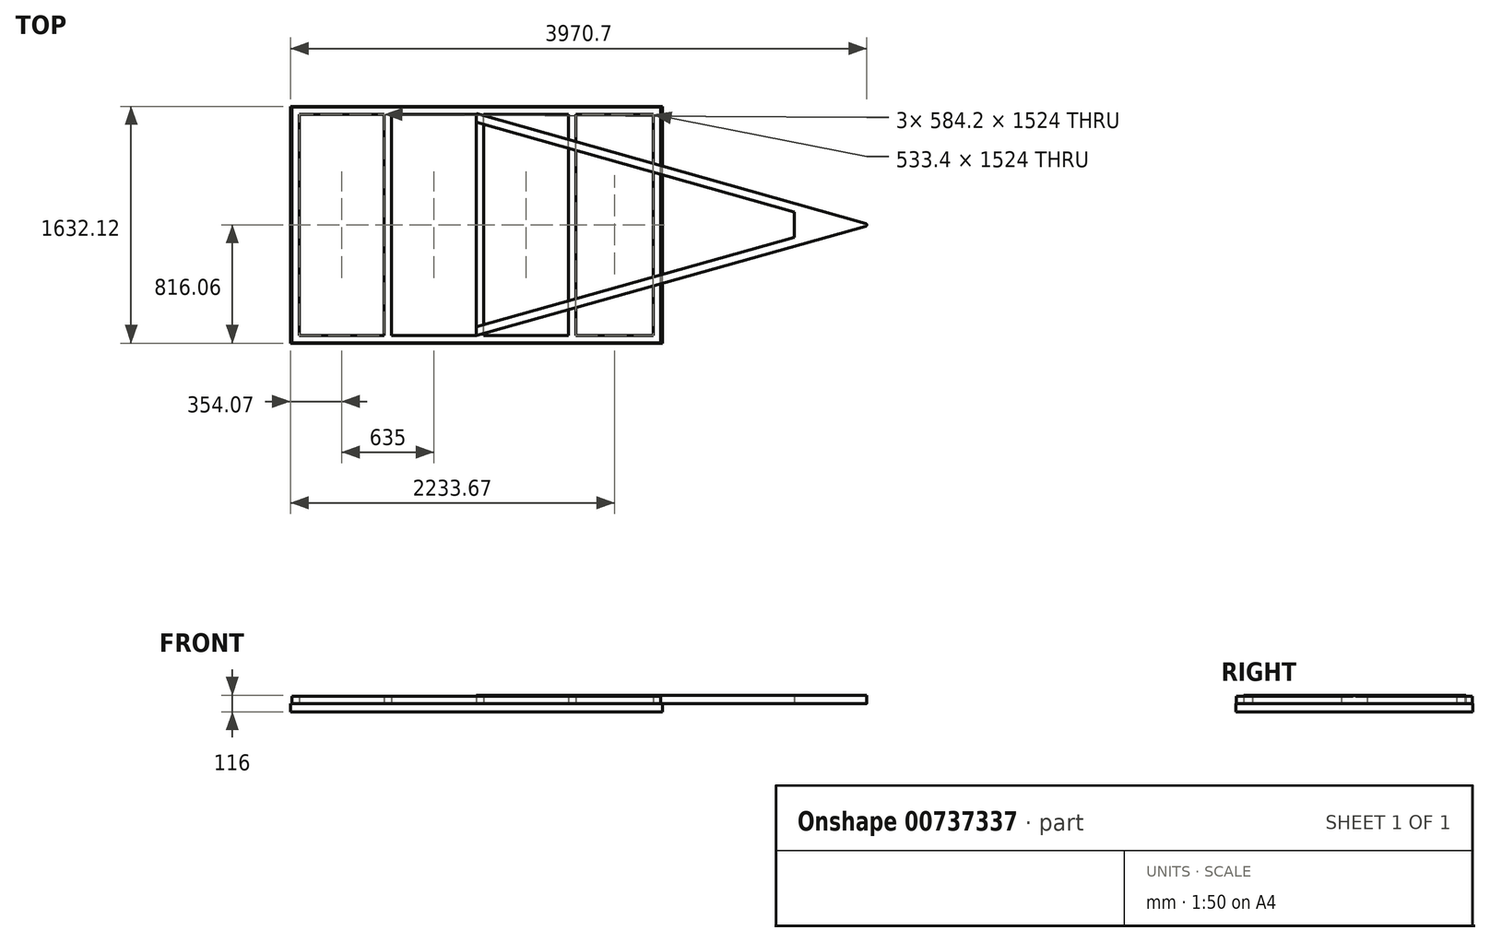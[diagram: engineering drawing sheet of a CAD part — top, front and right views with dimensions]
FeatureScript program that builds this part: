
annotation { "Feature Type Name" : "Feature", "Feature Type Description" : "" }
export const myFeature = defineFeature(function(context is Context, id is Id, definition is map)
    precondition{}
    {
        {
            var Q0;
            Q0=qCreatedBy(makeId("Top.planeOp"),FACE);
            var sketch = newSketch(context, id + "F0", { "sketchPlane" : qUnion([Q0])});
            skLineSegment(sketch, "E0.bottom", {"start": v(1219.2, -762) * mm, "end": v(-1219.2, -762) * mm});
            skLineSegment(sketch, "E0.top", {"start": v(1219.2, 762) * mm, "end": v(-1219.2, 762) * mm});
            skLineSegment(sketch, "E0.left", {"start": v(1219.2, -762) * mm, "end": v(1219.2, 762) * mm});
            skLineSegment(sketch, "E0.right", {"start": v(-1219.2, -762) * mm, "end": v(-1219.2, 762) * mm});
            skPoint(sketch, "E0.middle", {"position": v(0, 0) * mm});
            skLineSegment(sketch, "E1.0", {"start": v(1270, 812.8) * mm, "end": v(-1270, 812.8) * mm});
            skLineSegment(sketch, "E1.1", {"start": v(1270, -812.8) * mm, "end": v(1270, 812.8) * mm});
            skLineSegment(sketch, "E1.2", {"start": v(1270, -812.8) * mm, "end": v(-1270, -812.8) * mm});
            skLineSegment(sketch, "E1.3", {"start": v(-1270, -812.8) * mm, "end": v(-1270, 812.8) * mm});
            skPoint(sketch, "E2.orphan", {"position": v(0, -762) * mm});
            skPoint(sketch, "E3.end.orphan", {"position": v(0, 762) * mm});
            skLineSegment(sketch, "E4", {"start": v(-635, 762) * mm, "end": v(-635, -762) * mm});
            skLineSegment(sketch, "E5", {"start": v(-584.2, 762) * mm, "end": v(-584.2, -762) * mm});
            skLineSegment(sketch, "E6", {"start": v(-635, -762) * mm, "end": v(-584.2, -762) * mm});
            skLineSegment(sketch, "E7", {"start": v(-635, 762) * mm, "end": v(-584.2, 762) * mm});
            skLineSegment(sketch, "E8.bottom", {"start": v(50.8, -762) * mm, "end": v(0, -762) * mm});
            skLineSegment(sketch, "E8.top", {"start": v(50.8, 762) * mm, "end": v(0, 762) * mm});
            skLineSegment(sketch, "E8.left", {"start": v(50.8, -762) * mm, "end": v(50.8, 762) * mm});
            skLineSegment(sketch, "E8.right", {"start": v(0, -762) * mm, "end": v(0, 762) * mm});
            skLineSegment(sketch, "E9.bottom", {"start": v(635, -762) * mm, "end": v(685.8, -762) * mm});
            skLineSegment(sketch, "E9.top", {"start": v(635, 762) * mm, "end": v(685.8, 762) * mm});
            skLineSegment(sketch, "E9.left", {"start": v(635, -762) * mm, "end": v(635, 762) * mm});
            skLineSegment(sketch, "E9.right", {"start": v(685.8, -762) * mm, "end": v(685.8, 762) * mm});
            skLineSegment(sketch, "E10", {"start": v(0, 0) * mm, "end": v(2700, 0) * mm, "construction": true});
            skPoint(sketch, "E11.0.midPoint", {"position": v(1345.71, 381) * mm});
            skPoint(sketch, "E12.orphan", {"position": v(2005.62, 0) * mm});
            skSolve(sketch);
        }
        {
            var Q0;
            {var subQ20=sQuery(id+"F0.wireOp",EDGE,"E0.left");Q0=makeQuery(id+"F0.imprint","IMPRINT",FACE,{"disambiguationData":[TD([[makeQuery(id+"F0.imprint","IMPRINT",EDGE,{"derivedFrom":subQ20}),-1.0]])]});}
            var Q1;
            {var subQ0=sQuery(id+"F0.wireOp",EDGE,"E4");Q1=makeQuery(id+"F0.imprint","IMPRINT",FACE,{"disambiguationData":[TD([[makeQuery(id+"F0.imprint","IMPRINT",EDGE,{"derivedFrom":subQ0}),1.0]])]});}
            var Q2;
            {var subQ0=sQuery(id+"F0.wireOp",EDGE,"E8.left");Q2=makeQuery(id+"F0.imprint","IMPRINT",FACE,{"disambiguationData":[TD([[makeQuery(id+"F0.imprint","IMPRINT",EDGE,{"derivedFrom":subQ0}),1.0]])]});}
            var Q3;
            {var subQ0=sQuery(id+"F0.wireOp",EDGE,"E9.left");Q3=makeQuery(id+"F0.imprint","IMPRINT",FACE,{"disambiguationData":[TD([[makeQuery(id+"F0.imprint","IMPRINT",EDGE,{"derivedFrom":subQ0}),-1.0]])]});}
            extrude(context, id + "F1", {"entities" : qUnion([Q0, Q1, Q2, Q3]), "depth" : 50.8 * mm, "offsetDistance" : 25 * mm});
        }
        {
            var Q0;
            Q0=qCreatedBy(makeId("Top.planeOp"),FACE);
            var sketch = newSketch(context, id + "F2", { "sketchPlane" : qUnion([Q0])});
            skLineSegment(sketch, "E13", {"start": v(2716.43, 0) * mm, "end": v(0, -762) * mm});
            skLineSegment(sketch, "E14", {"start": v(0, 767.48) * mm, "end": v(2716.43, 0) * mm});
            skLineSegment(sketch, "E15.0", {"start": v(2500.92, 0.2) * mm, "end": v(0, -701.35) * mm});
            skLineSegment(sketch, "E15.1", {"start": v(0, 706.8) * mm, "end": v(2500.92, 0.2) * mm});
            skLineSegment(sketch, "E16", {"start": v(0, 767.48) * mm, "end": v(0, 706.8) * mm});
            skLineSegment(sketch, "E17", {"start": v(2189.72, -87.1) * mm, "end": v(2189.72, 88.13) * mm});
            skLineSegment(sketch, "E18.trimOffspring", {"start": v(0, -701.35) * mm, "end": v(0, -762) * mm});
            skSolve(sketch);
        }
        {
            var Q0;
            {var subQ8=sQuery(id+"F2.wireOp",EDGE,"E13");Q0=makeQuery(id+"F2.imprint","IMPRINT",FACE,{"disambiguationData":[TD([[makeQuery(id+"F2.imprint","IMPRINT",EDGE,{"derivedFrom":subQ8}),-1.0]])]});}
            var Q1;
            {var subQ3=sQuery(id+"F2.wireOp",EDGE,"E17");Q1=makeQuery(id+"F2.imprint","IMPRINT",FACE,{"disambiguationData":[TD([[makeQuery(id+"F2.imprint","IMPRINT",EDGE,{"derivedFrom":subQ3}),-1.0]])]});}
            extrude(context, id + "F3", {"entities" : qUnion([Q0, Q1]), "depth" : 58 * mm, "offsetDistance" : 25 * mm});
        }
        {
            var Q0;
            Q0=makeQuery(id+"F3.opExtrude","SWEPT_EDGE",EDGE,{"disambiguationData":[OSD([sQuery(id+"F2.wireOp",EDGE,"E13"),sQuery(id+"F2.wireOp",EDGE,"E14")])]});
            fillet(context, id + "F4", {"entities" : qUnion([Q0]), "radius" : 10 * mm, "tangentPropagation" : true, "allowEdgeOverflow" : false});
        }
        {
            var Q0;
            Q0=qCreatedBy(makeId("Top.planeOp"),FACE);
            var sketch = newSketch(context, id + "F5", { "sketchPlane" : qUnion([Q0])});
            skLineSegment(sketch, "E19.bottom", {"start": v(1281.17, -816.06) * mm, "end": v(-1281.17, -816.06) * mm});
            skLineSegment(sketch, "E19.top", {"start": v(1281.17, 816.06) * mm, "end": v(-1281.17, 816.06) * mm});
            skLineSegment(sketch, "E19.left", {"start": v(1281.17, -816.06) * mm, "end": v(1281.17, 816.06) * mm});
            skLineSegment(sketch, "E19.right", {"start": v(-1281.17, -816.06) * mm, "end": v(-1281.17, 816.06) * mm});
            skPoint(sketch, "E19.middle", {"position": v(0, 0) * mm});
            skSolve(sketch);
        }
        {
            var Q0;
            Q0=makeQuery(id+"F5.imprint","IMPRINT",FACE,{"disambiguationData":[TD([[makeQuery(id+"F5.imprint","IMPRINT",EDGE,{"derivedFrom":sQuery(id+"F5.wireOp",EDGE,"E19.bottom")}),-1.0]])]});
            extrude(context, id + "F6", {"entities" : qUnion([Q0]), "oppositeDirection" : true, "depth" : 58 * mm, "offsetDistance" : 25 * mm});
        }
    });
